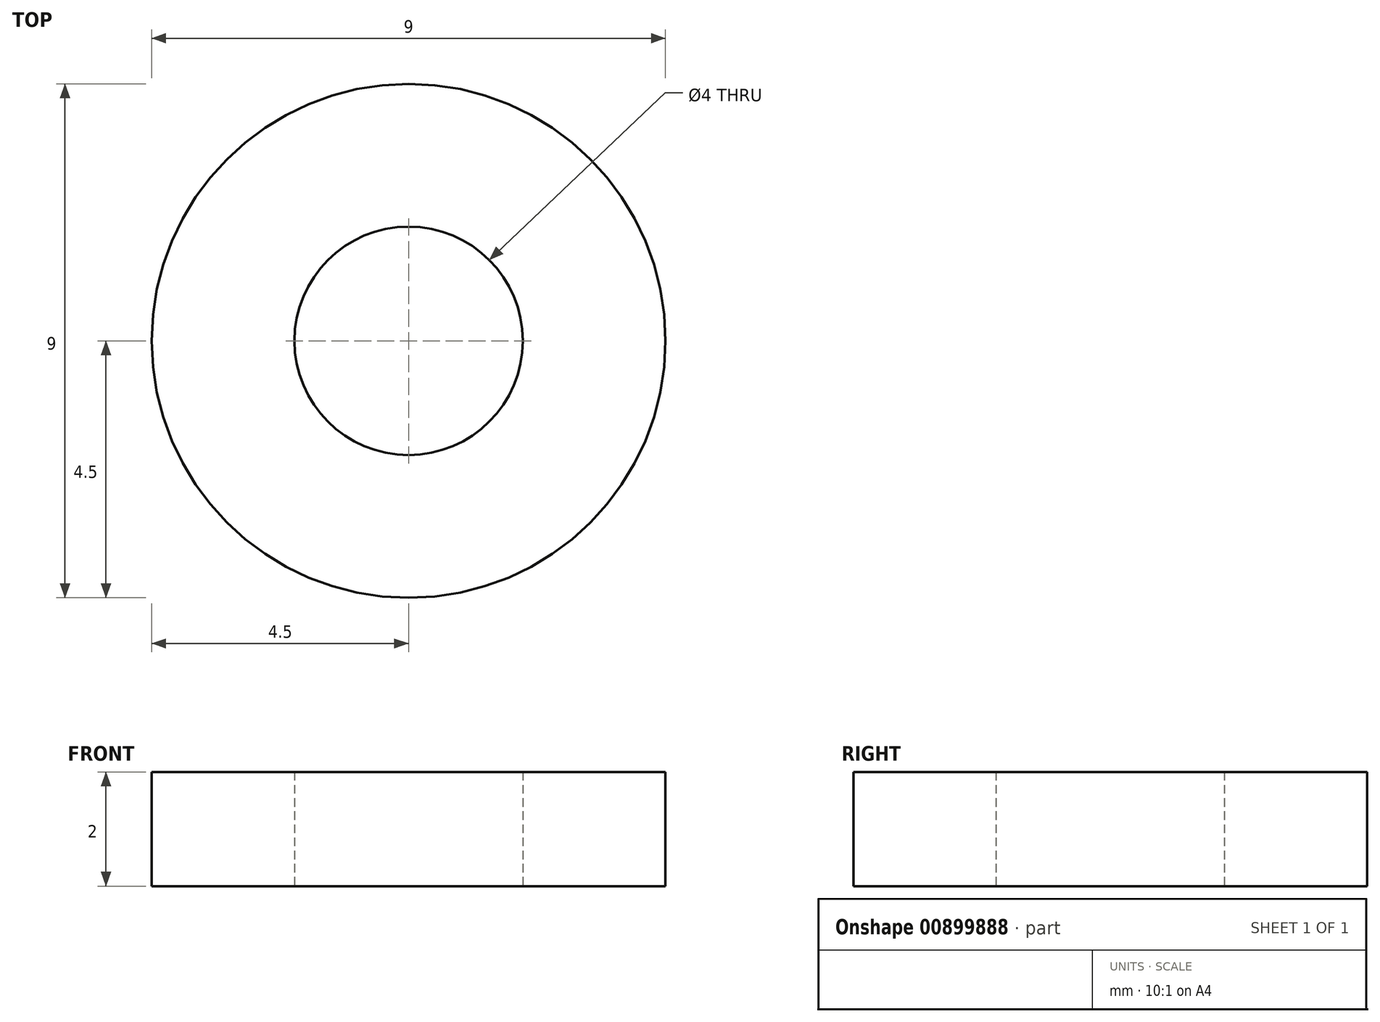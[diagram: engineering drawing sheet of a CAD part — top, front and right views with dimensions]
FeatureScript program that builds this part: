
annotation { "Feature Type Name" : "Feature", "Feature Type Description" : "" }
export const myFeature = defineFeature(function(context is Context, id is Id, definition is map)
    precondition{}
    {
        {
            var Q0;
            Q0=qCreatedBy(makeId("Top.planeOp"),FACE);
            var sketch = newSketch(context, id + "F0", { "sketchPlane" : qUnion([Q0])});
            skCircle(sketch, "E0", {"center": v(0, 0) * mm, "radius": 2 * mm});
            skCircle(sketch, "E1", {"center": v(0, 0) * mm, "radius": 4.5 * mm});
            skSolve(sketch);
        }
        {
            var Q0;
            Q0 = qSketchRegion(id + "F0", true);
            extrude(context, id + "F1", {"entities" : qUnion([Q0]), "depth" : 2 * mm, "offsetDistance" : 25 * mm});
        }
    });
